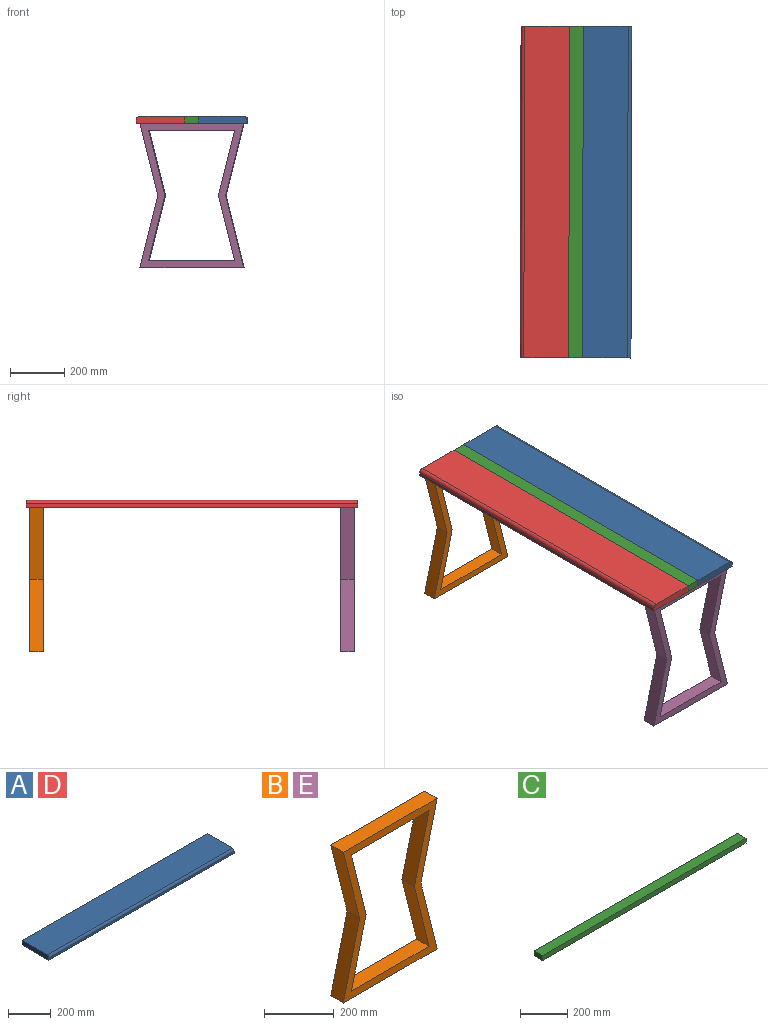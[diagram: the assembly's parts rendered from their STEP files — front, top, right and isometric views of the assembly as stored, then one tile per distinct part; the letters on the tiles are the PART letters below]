
ASSEMBLY  parts=5 mates=4
PART A: 7 faces, bbox 1219.2x177.8x25.4 mm
  f0: plane 177.8x25.4mm, normal (-1,0,0), area 4481.5mm2, adj f1,f3,f4,f5,f6
  f1: plane 1219.2x12.7mm, normal (0,-1,0), area 15483.8mm2, adj f0,f2,f5,f6
  f2: plane 177.8x25.4mm, normal (1,0,0), area 4481.5mm2, adj f1,f3,f4,f5,f6
  f3: plane 1219.2x25.4mm, normal (0,1,0), area 30967.7mm2, adj f0,f2,f4,f5
  f4: plane 1219.2x165.1mm, normal (0,0,1), area 201289.9mm2, adj f0,f2,f3,f6
  f5: plane 1219.2x177.8mm, normal (0,0,-1), area 216773.8mm2, adj f0,f1,f2,f3
  f6: cylinder r=12.7mm len=1219.2mm, axis (-1,0,0), area 24322mm2, adj f0,f1,f2,f4
PART B: 14 faces, bbox 381x50.8x529.9 mm
  f0: plane 239.54x59.72mm, normal (0.97,0,0.24), area 12541.1mm2, adj f1,f11,f12,f13
  f1: plane 315.98x50.8mm, normal (0,0,-1), area 16051.7mm2, adj f0,f2,f12,f13
  f2: plane 239.54x59.72mm, normal (-0.97,0,0.24), area 12541.1mm2, adj f1,f3,f12,f13
  f3: plane 239.54x59.72mm, normal (-0.97,0,-0.24), area 12541.1mm2, adj f2,f4,f12,f13
  f4: plane 315.98x50.8mm, normal (0,0,1), area 16051.7mm2, adj f3,f11,f12,f13
  f5: plane 381x50.8mm, normal (0,0,1), area 19354.8mm2, adj f6,f10,f12,f13
  f6: plane 264.94x66.06mm, normal (-0.97,0,-0.24), area 13870.9mm2, adj f5,f7,f12,f13
  f7: plane 264.94x66.06mm, normal (-0.97,0,0.24), area 13870.9mm2, adj f6,f8,f12,f13
  f8: plane 381x50.8mm, normal (0,0,-1), area 19354.8mm2, adj f7,f9,f12,f13
  f9: plane 264.94x66.06mm, normal (0.97,0,0.24), area 13870.9mm2, adj f8,f10,f12,f13
  f10: plane 264.94x66.06mm, normal (0.97,0,-0.24), area 13870.9mm2, adj f5,f9,f12,f13
  f11: plane 239.54x59.72mm, normal (0.97,0,-0.24), area 12541.1mm2, adj f0,f4,f12,f13
  f12: plane 529.88x381mm, normal (0,-1,0), area 44115.3mm2, adj f0,f1,f2,f3,f4,f5,f6,f7
  f13: plane 529.88x381mm, normal (0,1,0), area 44115.3mm2, adj f0,f1,f2,f3,f4,f5,f6,f7
PART C: 6 faces, bbox 1219.2x50.8x25.4 mm
  f0: plane 50.8x25.4mm, normal (-1,0,0), area 1290.3mm2, adj f1,f3,f4,f5
  f1: plane 1219.2x25.4mm, normal (0,-1,0), area 30967.7mm2, adj f0,f2,f4,f5
  f2: plane 50.8x25.4mm, normal (1,0,0), area 1290.3mm2, adj f1,f3,f4,f5
  f3: plane 1219.2x25.4mm, normal (0,1,0), area 30967.7mm2, adj f0,f2,f4,f5
  f4: plane 1219.2x50.8mm, normal (0,0,1), area 61935.4mm2, adj f0,f1,f2,f3
  f5: plane 1219.2x50.8mm, normal (0,0,-1), area 61935.4mm2, adj f0,f1,f2,f3
PART D: same geometry as A
PART E: same geometry as B
PLACE A rot(axis=(0,0,1),89.9deg) t=(1889.66,-1058.3,-191.06)mm
PLACE B rot(axis=(0,0,-1),0.1deg) t=(1753.02,-439.72,-442.68)mm
PLACE C rot(axis=(0,0,1),89.9deg) t=(1642.45,-1010.42,-191.06)mm
PLACE D rot(axis=(0,0,-1),90.1deg) t=(1568,-1014.84,-191.06)mm
PLACE E rot(axis=(0,0,-1),0.1deg) t=(1750.74,-1582.72,-442.68)mm
MATE fastened B.f5 <-> C.f5  axis (0,0,1) through (1730.02,-439.67,-191.06)mm
MATE fastened C.f1 <-> A.f3  axis (1,0,0) through (1755.45,-427.03,-165.66)mm
MATE fastened D.f3 <-> C.f3  axis (1,0,0) through (1703.43,-1036.52,-178.36)mm
MATE fastened E.f5 <-> C.f5  axis (0,0,1) through (1727.63,-1633.47,-191.06)mm
